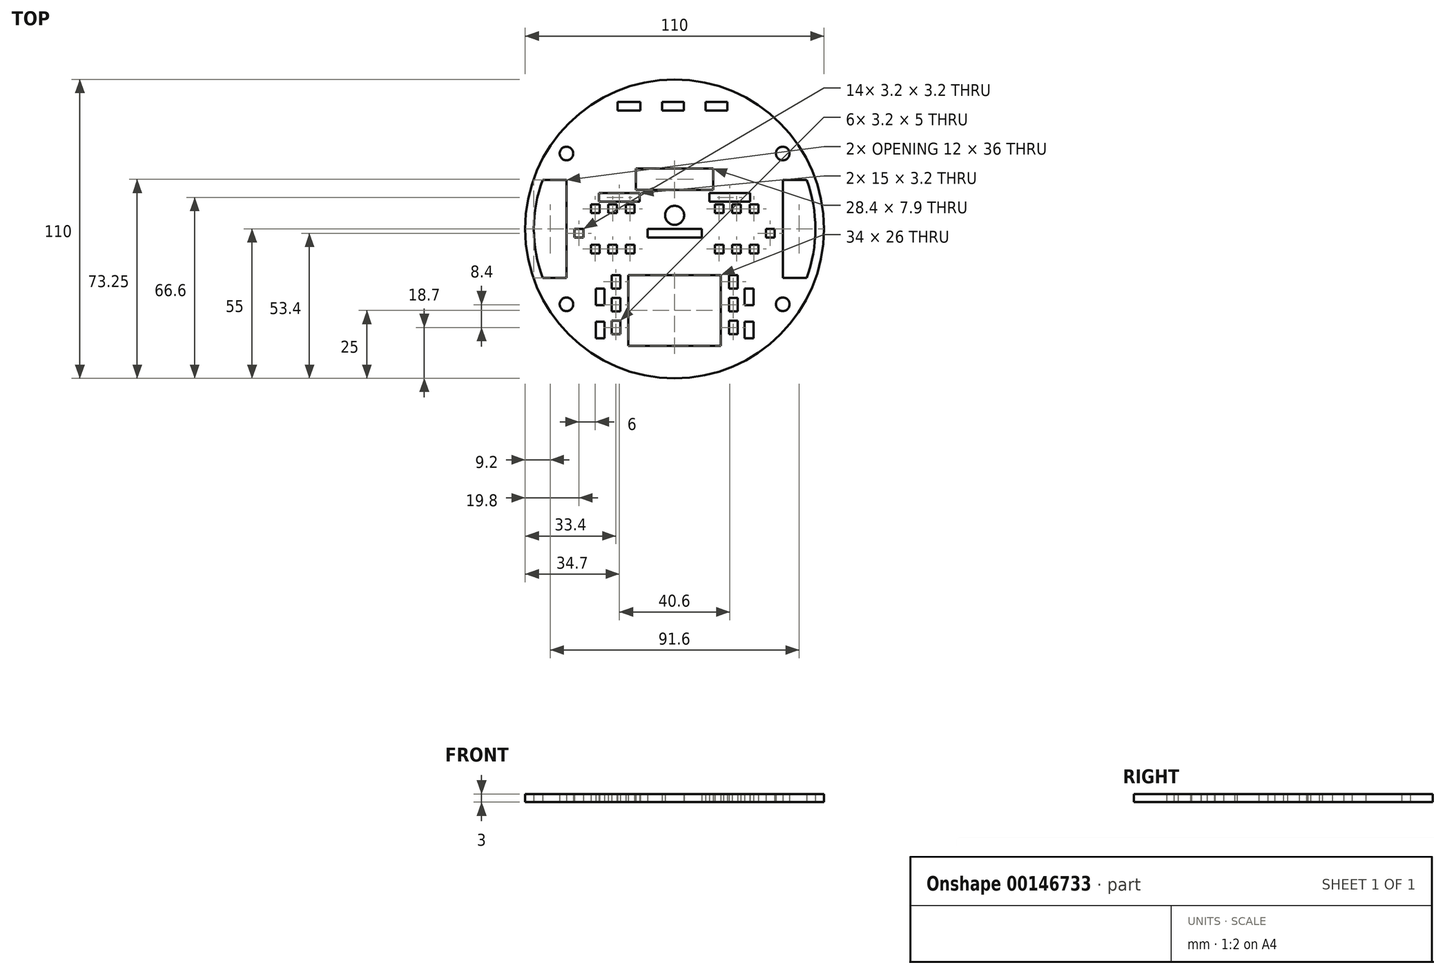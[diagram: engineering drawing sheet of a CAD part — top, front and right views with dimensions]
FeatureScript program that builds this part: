
annotation { "Feature Type Name" : "Feature", "Feature Type Description" : "" }
export const myFeature = defineFeature(function(context is Context, id is Id, definition is map)
    precondition{}
    {
        {
            var Q0;
            Q0=qCreatedBy(makeId("Top.planeOp"),FACE);
            var sketch = newSketch(context, id + "F0", { "sketchPlane" : qUnion([Q0])});
            skPoint(sketch, "E0.middle", {"position": v(0, 0) * mm});
            skLineSegment(sketch, "E1.MirrorCS", {"start": v(-12.59, 43.5) * mm, "end": v(-21, 43.5) * mm});
            skLineSegment(sketch, "E2.MirrorCS", {"start": v(-12.59, 43.5) * mm, "end": v(-4.59, 43.5) * mm, "construction": true});
            skLineSegment(sketch, "E3.MirrorCS", {"start": v(-4.59, 43.5) * mm, "end": v(-4.59, 46.7) * mm});
            skLineSegment(sketch, "E4.MirrorCS", {"start": v(3.41, 43.5) * mm, "end": v(-4.59, 43.5) * mm});
            skLineSegment(sketch, "E5.MirrorCS", {"start": v(3.41, 43.5) * mm, "end": v(11.41, 43.5) * mm, "construction": true});
            skLineSegment(sketch, "E6.MirrorCS", {"start": v(19.41, 43.5) * mm, "end": v(11.41, 43.5) * mm});
            skLineSegment(sketch, "E7.MirrorCS", {"start": v(-21, 43.5) * mm, "end": v(-21, 46.7) * mm});
            skLineSegment(sketch, "E8.MirrorCS", {"start": v(-12.59, 46.7) * mm, "end": v(-12.59, 43.5) * mm});
            skLineSegment(sketch, "E9.MirrorCS", {"start": v(-4.59, 46.7) * mm, "end": v(3.41, 46.7) * mm});
            skLineSegment(sketch, "E10.MirrorCS", {"start": v(3.41, 46.7) * mm, "end": v(3.41, 43.5) * mm});
            skLineSegment(sketch, "E11.MirrorCS", {"start": v(11.41, 43.5) * mm, "end": v(11.41, 46.7) * mm});
            skLineSegment(sketch, "E12.MirrorCS", {"start": v(19.41, 46.7) * mm, "end": v(19.41, 43.5) * mm});
            skLineSegment(sketch, "E13.MirrorCS", {"start": v(11.41, 46.7) * mm, "end": v(19.41, 46.7) * mm});
            skLineSegment(sketch, "E14.MirrorCS", {"start": v(-21, 46.7) * mm, "end": v(-12.59, 46.7) * mm});
            skArc(sketch, "E15", {"start": v(-51.97, -18) * mm, "mid": v(55, 0) * mm, "end": v(-51.97, 18) * mm, "construction": true});
            skLineSegment(sketch, "E16", {"start": v(-55, 0) * mm, "end": v(-39.8, 0) * mm, "construction": true});
            skLineSegment(sketch, "E17", {"start": v(-39.8, 0) * mm, "end": v(-39.8, 18) * mm, "construction": true});
            skLineSegment(sketch, "E18", {"start": v(-39.8, 18) * mm, "end": v(-39.8, -18) * mm, "construction": true});
            skLineSegment(sketch, "E19", {"start": v(-39.8, 0) * mm, "end": v(-30.8, 0) * mm, "construction": true});
            skLineSegment(sketch, "E20", {"start": v(-30.8, 0) * mm, "end": v(-30.8, 9) * mm, "construction": true});
            skLineSegment(sketch, "E21", {"start": v(-30.8, 0) * mm, "end": v(-24.4, 0) * mm, "construction": true});
            skLineSegment(sketch, "E22", {"start": v(-24.4, 0) * mm, "end": v(-18, 0) * mm, "construction": true});
            skLineSegment(sketch, "E23", {"start": v(-30.8, 9) * mm, "end": v(-18, 9) * mm, "construction": true});
            skLineSegment(sketch, "E24", {"start": v(-24.4, 0) * mm, "end": v(-24.4, 9) * mm, "construction": true});
            skLineSegment(sketch, "E25", {"start": v(-18, 0) * mm, "end": v(-18, 9) * mm, "construction": true});
            skLineSegment(sketch, "E26.bottom", {"start": v(-30.8, 9) * mm, "end": v(-27.6, 9) * mm});
            skLineSegment(sketch, "E26.top", {"start": v(-30.8, 5.8) * mm, "end": v(-27.6, 5.8) * mm});
            skLineSegment(sketch, "E26.left", {"start": v(-30.8, 9) * mm, "end": v(-30.8, 5.8) * mm});
            skLineSegment(sketch, "E26.right", {"start": v(-27.6, 9) * mm, "end": v(-27.6, 5.8) * mm});
            skLineSegment(sketch, "E27.bottom", {"start": v(-24.4, 9) * mm, "end": v(-21.2, 9) * mm});
            skLineSegment(sketch, "E27.top", {"start": v(-24.4, 5.8) * mm, "end": v(-21.2, 5.8) * mm});
            skLineSegment(sketch, "E27.left", {"start": v(-24.4, 9) * mm, "end": v(-24.4, 5.8) * mm});
            skLineSegment(sketch, "E27.right", {"start": v(-21.2, 9) * mm, "end": v(-21.2, 5.8) * mm});
            skLineSegment(sketch, "E28.bottom", {"start": v(-18, 9) * mm, "end": v(-14.8, 9) * mm});
            skLineSegment(sketch, "E28.top", {"start": v(-18, 5.8) * mm, "end": v(-14.8, 5.8) * mm});
            skLineSegment(sketch, "E28.left", {"start": v(-18, 9) * mm, "end": v(-18, 5.8) * mm});
            skLineSegment(sketch, "E28.right", {"start": v(-14.8, 9) * mm, "end": v(-14.8, 5.8) * mm});
            skLineSegment(sketch, "E29", {"start": v(-55, 0) * mm, "end": v(0, 0) * mm, "construction": true});
            skLineSegment(sketch, "E30.MirrorCS", {"start": v(-30.8, -9) * mm, "end": v(-27.6, -9) * mm});
            skLineSegment(sketch, "E31.MirrorCS", {"start": v(-30.8, -9) * mm, "end": v(-30.8, -5.8) * mm});
            skLineSegment(sketch, "E32.MirrorCS", {"start": v(-27.6, -9) * mm, "end": v(-27.6, -5.8) * mm});
            skLineSegment(sketch, "E33.MirrorCS", {"start": v(-24.4, -9) * mm, "end": v(-21.2, -9) * mm});
            skLineSegment(sketch, "E34.MirrorCS", {"start": v(-24.4, -9) * mm, "end": v(-24.4, -5.8) * mm});
            skLineSegment(sketch, "E35.MirrorCS", {"start": v(-18, -9) * mm, "end": v(-18, -5.8) * mm});
            skLineSegment(sketch, "E36.MirrorCS", {"start": v(-14.8, -9) * mm, "end": v(-14.8, -5.8) * mm});
            skLineSegment(sketch, "E37.MirrorCS", {"start": v(-24.4, 0) * mm, "end": v(-24.4, -9) * mm, "construction": true});
            skLineSegment(sketch, "E38.MirrorCS", {"start": v(-30.8, -9) * mm, "end": v(-18, -9) * mm, "construction": true});
            skLineSegment(sketch, "E39.MirrorCS", {"start": v(-18, 0) * mm, "end": v(-18, -9) * mm, "construction": true});
            skLineSegment(sketch, "E40.MirrorCS", {"start": v(-30.8, -5.8) * mm, "end": v(-27.6, -5.8) * mm});
            skLineSegment(sketch, "E41.MirrorCS", {"start": v(-24.4, -5.8) * mm, "end": v(-21.2, -5.8) * mm});
            skLineSegment(sketch, "E42.MirrorCS", {"start": v(-18, -9) * mm, "end": v(-14.8, -9) * mm});
            skLineSegment(sketch, "E43.MirrorCS", {"start": v(-21.2, -9) * mm, "end": v(-21.2, -5.8) * mm});
            skLineSegment(sketch, "E44.MirrorCS", {"start": v(-18, -5.8) * mm, "end": v(-14.8, -5.8) * mm});
            skLineSegment(sketch, "E45.MirrorCS", {"start": v(-30.8, 0) * mm, "end": v(-30.8, -9) * mm, "construction": true});
            skLineSegment(sketch, "E46", {"start": v(-39.8, 18) * mm, "end": v(-44.8, 18) * mm});
            skLineSegment(sketch, "E47", {"start": v(-39.8, -18) * mm, "end": v(-44.8, -18) * mm});
            skLineSegment(sketch, "E48", {"start": v(-44.8, 18) * mm, "end": v(-48.57, 18) * mm});
            skLineSegment(sketch, "E49", {"start": v(-44.8, -18) * mm, "end": v(-48.57, -18) * mm});
            skLineSegment(sketch, "E50", {"start": v(-39.8, 18) * mm, "end": v(-39.8, -18) * mm});
            skCircle(sketch, "E51", {"center": v(0, 0) * mm, "radius": 55 * mm});
            skLineSegment(sketch, "E52", {"start": v(0, 0) * mm, "end": v(-51.8, 0) * mm, "construction": true});
            skArc(sketch, "E53", {"start": v(-51.8, 0) * mm, "mid": v(-50.99, 9.14) * mm, "end": v(-48.57, 18) * mm});
            skArc(sketch, "E54", {"start": v(-51.8, 0) * mm, "mid": v(-50.99, -9.14) * mm, "end": v(-48.57, -18) * mm});
            skLineSegment(sketch, "E55.MirrorCS", {"start": v(39.8, 0) * mm, "end": v(30.8, 0) * mm, "construction": true});
            skLineSegment(sketch, "E56.MirrorCS", {"start": v(44.8, -18) * mm, "end": v(48.57, -18) * mm});
            skArc(sketch, "E57.MirrorCS", {"start": v(51.8, 0) * mm, "mid": v(50.99, -9.14) * mm, "end": v(48.57, -18) * mm});
            skArc(sketch, "E58.MirrorCS", {"start": v(51.8, 0) * mm, "mid": v(50.99, 9.14) * mm, "end": v(48.57, 18) * mm});
            skLineSegment(sketch, "E59.MirrorCS", {"start": v(44.8, 18) * mm, "end": v(48.57, 18) * mm});
            skLineSegment(sketch, "E60.MirrorCS", {"start": v(55, 0) * mm, "end": v(0, 0) * mm, "construction": true});
            skLineSegment(sketch, "E61.MirrorCS", {"start": v(39.8, 18) * mm, "end": v(39.8, -18) * mm});
            skLineSegment(sketch, "E62.MirrorCS", {"start": v(0, 0) * mm, "end": v(51.8, 0) * mm, "construction": true});
            skLineSegment(sketch, "E63.MirrorCS", {"start": v(39.8, 0) * mm, "end": v(39.8, 18) * mm, "construction": true});
            skLineSegment(sketch, "E64.MirrorCS", {"start": v(39.8, 18) * mm, "end": v(44.8, 18) * mm});
            skLineSegment(sketch, "E65.MirrorCS", {"start": v(39.8, -18) * mm, "end": v(44.8, -18) * mm});
            skLineSegment(sketch, "E66.MirrorCS", {"start": v(39.8, 18) * mm, "end": v(39.8, -18) * mm, "construction": true});
            skLineSegment(sketch, "E67.MirrorCS", {"start": v(55, 0) * mm, "end": v(39.8, 0) * mm, "construction": true});
            skLineSegment(sketch, "E68", {"start": v(-17, -24) * mm, "end": v(-17, -24) * mm});
            skLineSegment(sketch, "E69", {"start": v(0, 0) * mm, "end": v(-35.3, 0) * mm, "construction": true});
            skLineSegment(sketch, "E70", {"start": v(-17, -43) * mm, "end": v(-25.8, -43) * mm, "construction": true});
            skLineSegment(sketch, "E71.MirrorCS", {"start": v(17, -43) * mm, "end": v(25.8, -43) * mm, "construction": true});
            skLineSegment(sketch, "E72", {"start": v(-21, 43.5) * mm, "end": v(21, 43.5) * mm, "construction": true});
            skLineSegment(sketch, "E73", {"start": v(0, 0) * mm, "end": v(32.3, 0) * mm, "construction": true});
            skLineSegment(sketch, "E74", {"start": v(0, 0) * mm, "end": v(-36.8, 0) * mm, "construction": true});
            skLineSegment(sketch, "E75.bottom", {"start": v(-36.8, 0) * mm, "end": v(-33.6, 0) * mm});
            skLineSegment(sketch, "E75.top", {"start": v(-36.8, -3.2) * mm, "end": v(-33.6, -3.2) * mm});
            skLineSegment(sketch, "E75.left", {"start": v(-36.8, 0) * mm, "end": v(-36.8, -3.2) * mm});
            skLineSegment(sketch, "E75.right", {"start": v(-33.6, 0) * mm, "end": v(-33.6, -3.2) * mm});
            skLineSegment(sketch, "E76.MirrorCS", {"start": v(36.8, 0) * mm, "end": v(33.6, 0) * mm});
            skLineSegment(sketch, "E77.MirrorCS", {"start": v(0, 0) * mm, "end": v(36.8, 0) * mm, "construction": true});
            skLineSegment(sketch, "E78.MirrorCS", {"start": v(0, 0) * mm, "end": v(35.3, 0) * mm, "construction": true});
            skLineSegment(sketch, "E79.MirrorCS", {"start": v(33.6, 0) * mm, "end": v(33.6, -3.2) * mm});
            skLineSegment(sketch, "E80.MirrorCS", {"start": v(36.8, 0) * mm, "end": v(36.8, -3.2) * mm});
            skLineSegment(sketch, "E81.MirrorCS", {"start": v(36.8, -3.2) * mm, "end": v(33.6, -3.2) * mm});
            skLineSegment(sketch, "E82", {"start": v(0, 0) * mm, "end": v(-10, 0) * mm});
            skLineSegment(sketch, "E83", {"start": v(-10, 0) * mm, "end": v(-10, -3.2) * mm});
            skLineSegment(sketch, "E84", {"start": v(-10, -3.2) * mm, "end": v(10, -3.2) * mm});
            skLineSegment(sketch, "E85", {"start": v(10, -3.2) * mm, "end": v(10, 0) * mm});
            skLineSegment(sketch, "E86", {"start": v(10, 0) * mm, "end": v(-10, 0) * mm});
            skLineSegment(sketch, "E87", {"start": v(0, 0) * mm, "end": v(0, 5) * mm, "construction": true});
            skCircle(sketch, "E88", {"center": v(0, 5) * mm, "radius": 3.5 * mm});
            skLineSegment(sketch, "E89", {"start": v(0, 0) * mm, "end": v(0, 10) * mm, "construction": true});
            skLineSegment(sketch, "E90", {"start": v(0, 10) * mm, "end": v(-27.8, 10) * mm, "construction": true});
            skLineSegment(sketch, "E91.MirrorCS", {"start": v(30.8, 0) * mm, "end": v(24.4, 0) * mm, "construction": true});
            skLineSegment(sketch, "E92.MirrorCS", {"start": v(24.4, 0) * mm, "end": v(18, 0) * mm, "construction": true});
            skLineSegment(sketch, "E93.MirrorCS", {"start": v(24.4, -9) * mm, "end": v(24.4, -5.8) * mm});
            skLineSegment(sketch, "E94.MirrorCS", {"start": v(18, -9) * mm, "end": v(18, -5.8) * mm});
            skLineSegment(sketch, "E95.MirrorCS", {"start": v(30.8, 9) * mm, "end": v(30.8, 5.8) * mm});
            skLineSegment(sketch, "E96.MirrorCS", {"start": v(18, 9) * mm, "end": v(18, 5.8) * mm});
            skLineSegment(sketch, "E97.MirrorCS", {"start": v(24.4, 9) * mm, "end": v(21.2, 9) * mm});
            skLineSegment(sketch, "E98.MirrorCS", {"start": v(27.6, 9) * mm, "end": v(27.6, 5.8) * mm});
            skLineSegment(sketch, "E99.MirrorCS", {"start": v(24.4, 9) * mm, "end": v(24.4, 5.8) * mm});
            skLineSegment(sketch, "E100.MirrorCS", {"start": v(30.8, 9) * mm, "end": v(27.6, 9) * mm});
            skLineSegment(sketch, "E101.MirrorCS", {"start": v(24.4, -9) * mm, "end": v(21.2, -9) * mm});
            skLineSegment(sketch, "E102.MirrorCS", {"start": v(30.8, -9) * mm, "end": v(30.8, -5.8) * mm});
            skLineSegment(sketch, "E103.MirrorCS", {"start": v(30.8, -9) * mm, "end": v(27.6, -9) * mm});
            skLineSegment(sketch, "E104.MirrorCS", {"start": v(30.8, 0) * mm, "end": v(30.8, 9) * mm, "construction": true});
            skLineSegment(sketch, "E105.MirrorCS", {"start": v(24.4, 0) * mm, "end": v(24.4, 9) * mm, "construction": true});
            skLineSegment(sketch, "E106.MirrorCS", {"start": v(30.8, 5.8) * mm, "end": v(27.6, 5.8) * mm});
            skLineSegment(sketch, "E107.MirrorCS", {"start": v(21.2, -9) * mm, "end": v(21.2, -5.8) * mm});
            skLineSegment(sketch, "E108.MirrorCS", {"start": v(24.4, 0) * mm, "end": v(24.4, -9) * mm, "construction": true});
            skLineSegment(sketch, "E109.MirrorCS", {"start": v(14.8, -9) * mm, "end": v(14.8, -5.8) * mm});
            skLineSegment(sketch, "E110.MirrorCS", {"start": v(30.8, -9) * mm, "end": v(18, -9) * mm, "construction": true});
            skLineSegment(sketch, "E111.MirrorCS", {"start": v(24.4, 5.8) * mm, "end": v(21.2, 5.8) * mm});
            skLineSegment(sketch, "E112.MirrorCS", {"start": v(18, 0) * mm, "end": v(18, -9) * mm, "construction": true});
            skLineSegment(sketch, "E113.MirrorCS", {"start": v(18, -5.8) * mm, "end": v(14.8, -5.8) * mm});
            skLineSegment(sketch, "E114.MirrorCS", {"start": v(14.8, 9) * mm, "end": v(14.8, 5.8) * mm});
            skLineSegment(sketch, "E115.MirrorCS", {"start": v(30.8, -5.8) * mm, "end": v(27.6, -5.8) * mm});
            skLineSegment(sketch, "E116.MirrorCS", {"start": v(21.2, 9) * mm, "end": v(21.2, 5.8) * mm});
            skLineSegment(sketch, "E117.MirrorCS", {"start": v(24.4, -5.8) * mm, "end": v(21.2, -5.8) * mm});
            skLineSegment(sketch, "E118.MirrorCS", {"start": v(18, 9) * mm, "end": v(14.8, 9) * mm});
            skLineSegment(sketch, "E119.MirrorCS", {"start": v(18, -9) * mm, "end": v(14.8, -9) * mm});
            skLineSegment(sketch, "E120.MirrorCS", {"start": v(18, 5.8) * mm, "end": v(14.8, 5.8) * mm});
            skLineSegment(sketch, "E121.MirrorCS", {"start": v(30.8, 0) * mm, "end": v(30.8, -9) * mm, "construction": true});
            skLineSegment(sketch, "E122.MirrorCS", {"start": v(27.6, -9) * mm, "end": v(27.6, -5.8) * mm});
            skLineSegment(sketch, "E123.MirrorCS", {"start": v(18, 0) * mm, "end": v(18, 9) * mm, "construction": true});
            skLineSegment(sketch, "E124.MirrorCS", {"start": v(30.8, 9) * mm, "end": v(18, 9) * mm, "construction": true});
            skLineSegment(sketch, "E125.bottom", {"start": v(-27.8, 10) * mm, "end": v(-12.8, 10) * mm});
            skLineSegment(sketch, "E125.top", {"start": v(-27.8, 13.2) * mm, "end": v(-12.8, 13.2) * mm});
            skLineSegment(sketch, "E125.left", {"start": v(-27.8, 10) * mm, "end": v(-27.8, 13.2) * mm});
            skLineSegment(sketch, "E125.right", {"start": v(-12.8, 10) * mm, "end": v(-12.8, 13.2) * mm});
            skLineSegment(sketch, "E126", {"start": v(0, 55) * mm, "end": v(0, -55) * mm, "construction": true});
            skLineSegment(sketch, "E127.MirrorCS", {"start": v(27.8, 10) * mm, "end": v(27.8, 13.2) * mm});
            skLineSegment(sketch, "E128.MirrorCS", {"start": v(27.8, 13.2) * mm, "end": v(12.8, 13.2) * mm});
            skLineSegment(sketch, "E129.MirrorCS", {"start": v(27.8, 10) * mm, "end": v(12.8, 10) * mm});
            skLineSegment(sketch, "E130.MirrorCS", {"start": v(12.8, 10) * mm, "end": v(12.8, 13.2) * mm});
            skLineSegment(sketch, "E131", {"start": v(-12.8, 13.2) * mm, "end": v(12.8, 13.2) * mm, "construction": true});
            skLineSegment(sketch, "E132", {"start": v(0, 13.2) * mm, "end": v(0, 15.2) * mm, "construction": true});
            skLineSegment(sketch, "E133", {"start": v(14.2, 15.2) * mm, "end": v(14.2, 20.2) * mm, "construction": true});
            skLineSegment(sketch, "E134.top", {"start": v(14.2, 22.2) * mm, "end": v(-14.2, 22.2) * mm});
            skLineSegment(sketch, "E134.left", {"start": v(14.2, 15.2) * mm, "end": v(14.2, 22.2) * mm});
            skLineSegment(sketch, "E134.right", {"start": v(-14.2, 15.2) * mm, "end": v(-14.2, 22.2) * mm});
            skCircle(sketch, "E135", {"center": v(-39.8, -27.75) * mm, "radius": 2.5 * mm});
            skLineSegment(sketch, "E136", {"start": v(0, 0) * mm, "end": v(0, -30) * mm, "construction": true});
            skLineSegment(sketch, "E137", {"start": v(0, -30) * mm, "end": v(0, -17) * mm, "construction": true});
            skLineSegment(sketch, "E138", {"start": v(0, -17) * mm, "end": v(17, -17) * mm});
            skLineSegment(sketch, "E139", {"start": v(17, -17) * mm, "end": v(17, -43) * mm});
            skLineSegment(sketch, "E140", {"start": v(0, -17) * mm, "end": v(-17, -17) * mm});
            skLineSegment(sketch, "E141", {"start": v(-17, -17) * mm, "end": v(-17, -43) * mm});
            skLineSegment(sketch, "E142", {"start": v(-17, -43) * mm, "end": v(17, -43) * mm});
            skLineSegment(sketch, "E143", {"start": v(0, -55) * mm, "end": v(0, -40) * mm, "construction": true});
            skLineSegment(sketch, "E144", {"start": v(0, -40) * mm, "end": v(17, -40) * mm, "construction": true});
            skLineSegment(sketch, "E145", {"start": v(27.8, 10) * mm, "end": v(31, 10) * mm, "construction": true});
            skLineSegment(sketch, "E146", {"start": v(31, 10) * mm, "end": v(31, 45.43) * mm, "construction": true});
            skCircle(sketch, "E147.MirrorC", {"center": v(39.8, -27.75) * mm, "radius": 2.5 * mm});
            skCircle(sketch, "E148.MirrorC", {"center": v(39.8, 27.75) * mm, "radius": 2.5 * mm});
            skCircle(sketch, "E149.MirrorC", {"center": v(-39.8, 27.75) * mm, "radius": 2.5 * mm});
            skLineSegment(sketch, "E150", {"start": v(-14.2, 15.2) * mm, "end": v(-14.2, 14.3) * mm, "construction": true});
            skLineSegment(sketch, "E151", {"start": v(-14.2, 14.3) * mm, "end": v(14.2, 14.3) * mm});
            skLineSegment(sketch, "E152", {"start": v(14.2, 14.3) * mm, "end": v(14.2, 15.2) * mm});
            skLineSegment(sketch, "E153", {"start": v(-14.2, 14.3) * mm, "end": v(-14.2, 15.2) * mm});
            skLineSegment(sketch, "E154", {"start": v(-17, -17) * mm, "end": v(-20, -17) * mm, "construction": true});
            skLineSegment(sketch, "E155.bottom", {"start": v(-20, -17) * mm, "end": v(-23.2, -17) * mm});
            skLineSegment(sketch, "E155.top", {"start": v(-20, -22) * mm, "end": v(-23.2, -22) * mm});
            skLineSegment(sketch, "E155.left", {"start": v(-20, -17) * mm, "end": v(-20, -22) * mm});
            skLineSegment(sketch, "E155.right", {"start": v(-23.2, -17) * mm, "end": v(-23.2, -22) * mm});
            skLineSegment(sketch, "E156", {"start": v(-20, -17) * mm, "end": v(-20, -25.4) * mm, "construction": true});
            skLineSegment(sketch, "E157", {"start": v(-20, -25.4) * mm, "end": v(-20, -33.8) * mm, "construction": true});
            skLineSegment(sketch, "E158.bottom", {"start": v(-20, -25.4) * mm, "end": v(-23.2, -25.4) * mm});
            skLineSegment(sketch, "E158.top", {"start": v(-20, -30.4) * mm, "end": v(-23.2, -30.4) * mm});
            skLineSegment(sketch, "E158.left", {"start": v(-20, -25.4) * mm, "end": v(-20, -30.4) * mm});
            skLineSegment(sketch, "E158.right", {"start": v(-23.2, -25.4) * mm, "end": v(-23.2, -30.4) * mm});
            skLineSegment(sketch, "E159.bottom", {"start": v(-20, -33.8) * mm, "end": v(-23.2, -33.8) * mm});
            skLineSegment(sketch, "E159.top", {"start": v(-20, -38.8) * mm, "end": v(-23.2, -38.8) * mm});
            skLineSegment(sketch, "E159.left", {"start": v(-20, -33.8) * mm, "end": v(-20, -38.8) * mm});
            skLineSegment(sketch, "E159.right", {"start": v(-23.2, -33.8) * mm, "end": v(-23.2, -38.8) * mm});
            skLineSegment(sketch, "E160.MirrorCS", {"start": v(20, -25.4) * mm, "end": v(20, -30.4) * mm});
            skLineSegment(sketch, "E161.MirrorCS", {"start": v(20, -17) * mm, "end": v(20, -22) * mm});
            skLineSegment(sketch, "E162.MirrorCS", {"start": v(20, -22) * mm, "end": v(23.2, -22) * mm});
            skLineSegment(sketch, "E163.MirrorCS", {"start": v(20, -33.8) * mm, "end": v(23.2, -33.8) * mm});
            skLineSegment(sketch, "E164.MirrorCS", {"start": v(20, -30.4) * mm, "end": v(23.2, -30.4) * mm});
            skLineSegment(sketch, "E165.MirrorCS", {"start": v(20, -25.4) * mm, "end": v(23.2, -25.4) * mm});
            skLineSegment(sketch, "E166.MirrorCS", {"start": v(20, -25.4) * mm, "end": v(20, -33.8) * mm, "construction": true});
            skLineSegment(sketch, "E167.MirrorCS", {"start": v(20, -17) * mm, "end": v(20, -25.4) * mm, "construction": true});
            skLineSegment(sketch, "E168.MirrorCS", {"start": v(23.2, -17) * mm, "end": v(23.2, -22) * mm});
            skLineSegment(sketch, "E169.MirrorCS", {"start": v(20, -17) * mm, "end": v(23.2, -17) * mm});
            skLineSegment(sketch, "E170.MirrorCS", {"start": v(23.2, -33.8) * mm, "end": v(23.2, -38.8) * mm});
            skLineSegment(sketch, "E171.MirrorCS", {"start": v(20, -33.8) * mm, "end": v(20, -38.8) * mm});
            skLineSegment(sketch, "E172.MirrorCS", {"start": v(20, -38.8) * mm, "end": v(23.2, -38.8) * mm});
            skLineSegment(sketch, "E173.MirrorCS", {"start": v(23.2, -25.4) * mm, "end": v(23.2, -30.4) * mm});
            skCircle(sketch, "E174", {"center": v(0, 0) * mm, "radius": 51.8 * mm, "construction": true});
            skLineSegment(sketch, "E175", {"start": v(-29, -22) * mm, "end": v(-25.8, -22) * mm, "construction": true});
            skLineSegment(sketch, "E176.bottom", {"start": v(-29, -22) * mm, "end": v(-25.8, -22) * mm});
            skLineSegment(sketch, "E176.top", {"start": v(-29, -28.1) * mm, "end": v(-25.8, -28.1) * mm});
            skLineSegment(sketch, "E176.left", {"start": v(-29, -22) * mm, "end": v(-29, -28.1) * mm});
            skLineSegment(sketch, "E176.right", {"start": v(-25.8, -22) * mm, "end": v(-25.8, -28.1) * mm});
            skLineSegment(sketch, "E177", {"start": v(-29, -28.1) * mm, "end": v(-29, -34.2) * mm, "construction": true});
            skLineSegment(sketch, "E178.bottom", {"start": v(-29, -34.2) * mm, "end": v(-25.8, -34.2) * mm});
            skLineSegment(sketch, "E178.top", {"start": v(-29, -40.3) * mm, "end": v(-25.8, -40.3) * mm});
            skLineSegment(sketch, "E178.left", {"start": v(-29, -34.2) * mm, "end": v(-29, -40.3) * mm});
            skLineSegment(sketch, "E178.right", {"start": v(-25.8, -34.2) * mm, "end": v(-25.8, -40.3) * mm});
            skLineSegment(sketch, "E179.MirrorCS", {"start": v(29, -22) * mm, "end": v(25.8, -22) * mm});
            skLineSegment(sketch, "E180.MirrorCS", {"start": v(29, -22) * mm, "end": v(29, -28.1) * mm});
            skLineSegment(sketch, "E181.MirrorCS", {"start": v(25.8, -34.2) * mm, "end": v(25.8, -40.3) * mm});
            skLineSegment(sketch, "E182.MirrorCS", {"start": v(29, -34.2) * mm, "end": v(29, -40.3) * mm});
            skLineSegment(sketch, "E183.MirrorCS", {"start": v(29, -40.3) * mm, "end": v(25.8, -40.3) * mm});
            skLineSegment(sketch, "E184.MirrorCS", {"start": v(29, -34.2) * mm, "end": v(25.8, -34.2) * mm});
            skLineSegment(sketch, "E185.MirrorCS", {"start": v(29, -28.1) * mm, "end": v(29, -34.2) * mm, "construction": true});
            skLineSegment(sketch, "E186.MirrorCS", {"start": v(25.8, -22) * mm, "end": v(25.8, -28.1) * mm});
            skLineSegment(sketch, "E187.MirrorCS", {"start": v(29, -28.1) * mm, "end": v(25.8, -28.1) * mm});
            skLineSegment(sketch, "E188.MirrorCS", {"start": v(29, -22) * mm, "end": v(25.8, -22) * mm, "construction": true});
            skSolve(sketch);
        }
        {
            var Q0;
            Q0=qSketchRegion(id+"F0",true);
            extrude(context, id + "F1", {"entities" : qUnion([Q0]), "endBound" : BoundingType.SYMMETRIC, "depth" : 3 * mm});
        }
    });
